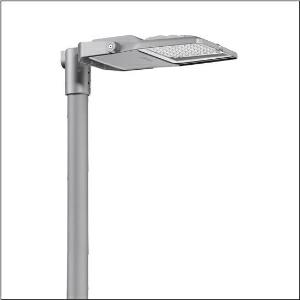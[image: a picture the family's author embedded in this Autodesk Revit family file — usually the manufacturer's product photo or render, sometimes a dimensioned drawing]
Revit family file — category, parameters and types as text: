
# Revit family: floodlight_fl_21_iq_mini___pl33t_5xa7771b2f3a_2789
name_source: partatom
category: Lighting Fixtures
units: mm (PartAtom-declared; Revit-internal decimal feet)

## family parameters
Cut with Voids When Loaded = No
Host = Face
Light Source = No
Part Type = Normal
Room Calculation Point = No
Round Connector Dimension = Use Diameter
Shared = No

## types (1)
- --- (1 x LED, 6170 lm, 45.5 W, 3000K)
    Apparent Load = 46 VA
    CIE Flux Codes = 26 75 99 100 100
    Color Rendering = 70
    Color Temperature = 3000K
    Default Elevation = 1800 mm
    Description = Floodlight FL 21 iQ mini, floodlight, primary light control with lens, of PMMA, primary optical cover: protective disc, of toughened safety glass, transparent, light distribution: PL33T, light emission: direct distribution, installation type: surface-mounted, LED, High Power LED, rated luminous flux: 6.170lm, luminous efficacy: 136lm/W, light colour: 730, colour temperature: 3000K, control: Auto-Match, Temp-Guard, Lumen-Switch, Night-Set, Smart-Wire, Light-Fading, Desk-Remote (wireless, voltage-free reading and setting of iQ features in the workshop via application-optimized NFC function/RFID function), optimised constant luminous flux control (CLO 2.0), with terminal, 6-pole, mains connection: 220..240V, AC, 50/60Hz, start of lifetime: 46W, end of service life: 48W, reduction: 22W, luminaire housing, of diecast aluminium, powder-coated, Siteco® metallic grey (DB 702S), corrosivity category C5 mid according to DIN EN ISO 12944, sealing non-destructively replaceable, please order mast flange separately, mast bracket, of steel, galvanised, powder-coated, Siteco® metallic grey (DB 702S), protection rating (complete): IP66, insulation class (complete): insulation class II (safety insulation), certification: CE, ENEC, VDE, protection symbol: D, impact resistance: IK08, permissible operating ambient temperature: -40..+40°C, permissible operating ambient temperature for outdoor applications: -40..+50°C, standard: DIN EN 12944, LABS conformity tested according to VDMA 24364:2018-05, packaging unit: 1 piece

Light Distribution: PL33T
    Height = 70 mm
    Lamp = 1 x LED
    Lamp Light Flux = 6170 lm
    Lamp Power = 45.5 W
    Lamp count = 1
    Length = 485 mm
    Luminous efficacy = 136 lm/W
    Manufacturer = Siteco
    ModVariant = No
    Model = 5XA7771B2F3A
    Number of Poles = 1
    OnlyDefault = Yes
    Power Factor = 1
    Product Name = Floodlight FL 21 iQ mini | PL33T
    Product group = floodlight | pylon annexe
    ProductGroupID = 6200
    Protection Class = Protection class II
    Protection Degree = IP 66
    RLX_Detail_Level = 1
    RLX_Emergency_Light_Flux = 0 lm
    RLX_Emergency_Type = 0
    RLX_Emergency_Type_DB = No
    RlxData = <blob elided: 101085 chars, md5=3dcc8589>
    Socket = socket
    Standby Power = 0 W
    System Light Flux = 6170 lm
    System Power = 46 W
    Type Comments = factory setting: luminous flux: 100 % | dim-lin: 254 | 463 mA
    Type Image = l_1007125.jpg
    URL = http://relux.com
    VarID = @adj_120617
    Voltage = 0 V
    Weight = 0.00 kg
    Width = 337 mm

## geometry (parser evidence)
native form markers: Blend x4, Sweep x13
no freeform markers — native parametric forms only
